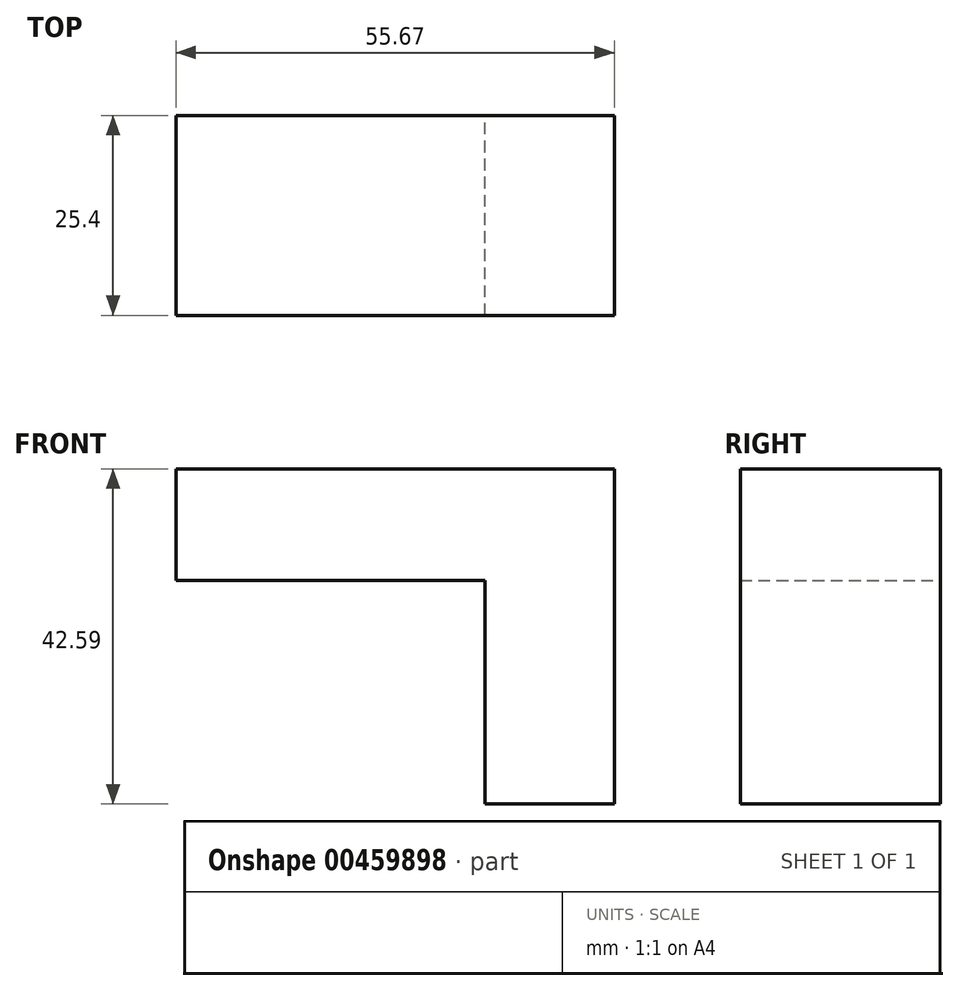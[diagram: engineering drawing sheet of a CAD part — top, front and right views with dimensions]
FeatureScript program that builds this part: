
annotation { "Feature Type Name" : "Feature", "Feature Type Description" : "" }
export const myFeature = defineFeature(function(context is Context, id is Id, definition is map)
    precondition{}
    {
        {
            var Q0;
            Q0=qCreatedBy(makeId("Front.planeOp"),FACE);
            var sketch = newSketch(context, id + "F0", { "sketchPlane" : qUnion([Q0])});
            skLineSegment(sketch, "E0", {"start": v(-51.8, 64.34) * mm, "end": v(-17.88, 64.34) * mm});
            skLineSegment(sketch, "E1", {"start": v(-17.88, 64.34) * mm, "end": v(3.87, 64.34) * mm});
            skLineSegment(sketch, "E2", {"start": v(3.87, 64.34) * mm, "end": v(3.87, 21.75) * mm});
            skLineSegment(sketch, "E3", {"start": v(3.87, 21.75) * mm, "end": v(-12.54, 21.75) * mm});
            skLineSegment(sketch, "E4", {"start": v(-12.54, 21.75) * mm, "end": v(-12.54, 50.14) * mm});
            skLineSegment(sketch, "E5", {"start": v(-12.54, 50.14) * mm, "end": v(-51.8, 50.14) * mm});
            skLineSegment(sketch, "E6", {"start": v(-51.8, 50.14) * mm, "end": v(-51.8, 64.34) * mm});
            skSolve(sketch);
        }
        {
            var Q0;
            Q0=makeQuery(id+"F0.imprint","IMPRINT",FACE,{"disambiguationData":[TD([[makeQuery(id+"F0.imprint","IMPRINT",EDGE,{"derivedFrom":sQuery(id+"F0.wireOp",EDGE,"E0")}),-1.0]])]});
            extrude(context, id + "F1", {"entities" : qUnion([Q0]), "depth" : 25.4 * mm});
        }
    });
